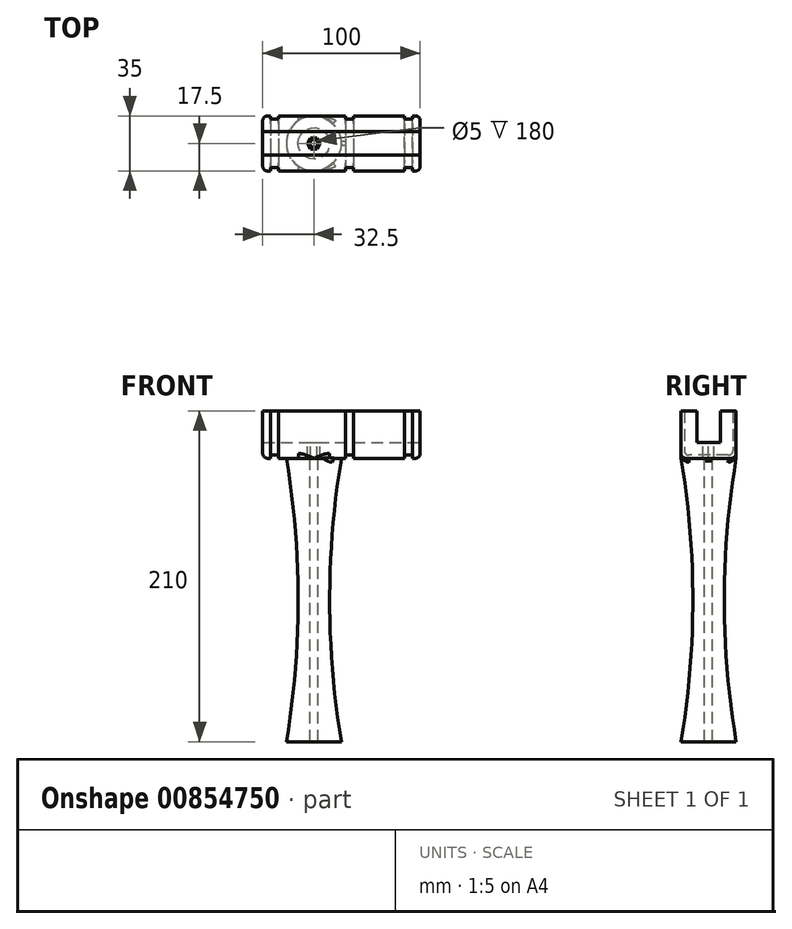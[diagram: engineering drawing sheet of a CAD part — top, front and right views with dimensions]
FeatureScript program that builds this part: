
annotation { "Feature Type Name" : "Feature", "Feature Type Description" : "" }
export const myFeature = defineFeature(function(context is Context, id is Id, definition is map)
    precondition{}
    {
        {
            var Q0;
            Q0=qCreatedBy(makeId("Front.planeOp"),FACE);
            var sketch = newSketch(context, id + "F0", { "sketchPlane" : qUnion([Q0])});
            skLineSegment(sketch, "E0.bottom", {"start": v(50, 15) * mm, "end": v(-50, 15) * mm});
            skLineSegment(sketch, "E0.top", {"start": v(50, -15) * mm, "end": v(-50, -15) * mm});
            skLineSegment(sketch, "E0.left", {"start": v(50, 15) * mm, "end": v(50, -15) * mm});
            skLineSegment(sketch, "E0.right", {"start": v(-50, 15) * mm, "end": v(-50, -15) * mm});
            skPoint(sketch, "E0.middle", {"position": v(0, 0) * mm});
            skLineSegment(sketch, "E1.bottom", {"start": v(-50, 15) * mm, "end": v(50, 15) * mm});
            skLineSegment(sketch, "E1.top", {"start": v(-50, -5) * mm, "end": v(50, -5) * mm});
            skLineSegment(sketch, "E1.left", {"start": v(-50, 15) * mm, "end": v(-50, -5) * mm});
            skLineSegment(sketch, "E1.right", {"start": v(50, 15) * mm, "end": v(50, -5) * mm});
            skSolve(sketch);
        }
        {
            var Q0;
            {var subQ0=sQuery(id+"F0.wireOp",EDGE,"E0.top");Q0=makeQuery(id+"F0.imprint","IMPRINT",FACE,{"disambiguationData":[TD([[makeQuery(id+"F0.imprint","IMPRINT",EDGE,{"derivedFrom":subQ0}),-1.0]])]});}
            var Q1;
            {var subQ0=sQuery(id+"F0.wireOp",EDGE,"E0.bottom");Q1=makeQuery(id+"F0.imprint","IMPRINT",FACE,{"disambiguationData":[TD([[makeQuery(id+"F0.imprint","IMPRINT",EDGE,{"derivedFrom":subQ0}),1.0]])]});}
            extrude(context, id + "F1", {"entities" : qUnion([Q0, Q1]), "endBound" : BoundingType.SYMMETRIC, "depth" : 35 * mm, "offsetDistance" : 25 * mm});
        }
        {
            var Q0;
            {var subQ0=sQuery(id+"F0.wireOp",EDGE,"E0.bottom");Q0=makeQuery(id+"F0.imprint","IMPRINT",FACE,{"disambiguationData":[TD([[makeQuery(id+"F0.imprint","IMPRINT",EDGE,{"derivedFrom":subQ0}),1.0]])]});}
            extrude(context, id + "F2", {"entities" : qUnion([Q0]), "operationType" : NewBodyOperationType.REMOVE, "endBound" : BoundingType.SYMMETRIC, "oppositeDirection" : true, "depth" : 15 * mm, "offsetDistance" : 25 * mm});
        }
        {
            var Q0;
            Q0=makeQuery(id+"F1.opExtrude","SWEPT_FACE",FACE,{"disambiguationData":[OSD([sQuery(id+"F0.wireOp",EDGE,"E0.top")])]});
            var sketch = newSketch(context, id + "F3", { "sketchPlane" : qUnion([Q0])});
            skCircle(sketch, "E2", {"center": v(-17.5, 0) * mm, "radius": 17.5 * mm});
            skPoint(sketch, "E3", {"position": v(-35, 0) * mm});
            skPoint(sketch, "E3.positionSnap0", {"position": v(-50, 0) * mm});
            skPoint(sketch, "E4", {"position": v(-42.5, 0) * mm});
            skLineSegment(sketch, "E5", {"start": v(-17.5, 0) * mm, "end": v(-17.5, 22.7) * mm, "construction": true});
            skPoint(sketch, "E6.MirrorP", {"position": v(7.5, 0) * mm});
            skPoint(sketch, "E7.MirrorP", {"position": v(42.5, 0) * mm});
            skSolve(sketch);
        }
        {
            var Q0;
            Q0=makeQuery(id+"F2.boolean.opBoolean","COPY",FACE,{"derivedFrom":makeQuery(id+"F2.opExtrude","SWEPT_FACE",FACE,{"disambiguationData":[OSD([sQuery(id+"F0.wireOp",EDGE,"E1.top")])]})});
            var sketch = newSketch(context, id + "F4", { "sketchPlane" : qUnion([Q0])});
            skPoint(sketch, "E8.0", {"position": v(-17.5, 0) * mm});
            skCircle(sketch, "E9", {"center": v(-17.5, 0) * mm, "radius": 2.5 * mm});
            skCircle(sketch, "E10.cCircle", {"center": v(-17.5, 0) * mm, "radius": 4 * mm, "construction": true});
            skLineSegment(sketch, "E10.0", {"start": v(-21.5, 0) * mm, "end": v(-19.5, 3.46) * mm});
            skLineSegment(sketch, "E10.1", {"start": v(-19.5, 3.46) * mm, "end": v(-15.5, 3.46) * mm});
            skLineSegment(sketch, "E10.2", {"start": v(-15.5, 3.46) * mm, "end": v(-13.5, 0) * mm});
            skLineSegment(sketch, "E10.3", {"start": v(-13.5, 0) * mm, "end": v(-15.5, -3.46) * mm});
            skLineSegment(sketch, "E10.4", {"start": v(-15.5, -3.46) * mm, "end": v(-19.5, -3.46) * mm});
            skLineSegment(sketch, "E10.5", {"start": v(-19.5, -3.46) * mm, "end": v(-21.5, 0) * mm});
            skSolve(sketch);
        }
        {
            var Q0;
            Q0=makeQuery(id+"F4.imprint","IMPRINT",FACE,{"disambiguationData":[TD([[makeQuery(id+"F4.imprint","IMPRINT",EDGE,{"derivedFrom":sQuery(id+"F4.wireOp",EDGE,"E9")}),-1.0]])]});
            extrude(context, id + "F5", {"entities" : qUnion([Q0]), "operationType" : NewBodyOperationType.REMOVE, "oppositeDirection" : true, "depth" : 10 * mm, "offsetDistance" : 25 * mm});
        }
        {
            var Q0;
            Q0=makeQuery(id+"F4.imprint","IMPRINT",FACE,{"disambiguationData":[TD([[makeQuery(id+"F4.imprint","IMPRINT",EDGE,{"derivedFrom":sQuery(id+"F4.wireOp",EDGE,"E9")}),1.0]])]});
            extrude(context, id + "F6", {"entities" : qUnion([Q0]), "operationType" : NewBodyOperationType.REMOVE, "endBound" : BoundingType.THROUGH_ALL, "oppositeDirection" : true, "depth" : 25 * mm, "offsetDistance" : 25 * mm});
        }
        {
            var Q0;
            {var subQ0=sQuery(id+"F3.wireOp",EDGE,"E2");var subQ1=sQuery(id+"F0.wireOp",EDGE,"E0.top");var subQ2=makeQuery(id+"F3.imprint","INTERSECT",VERTEX,{"derivedFrom":[makeQuery(id+"F1.opExtrude","CAP_EDGE",EDGE,{"disambiguationData":[OSD([subQ1])],"isStart":true}),subQ0]});Q0=makeQuery(id+"F3.imprint","IMPRINT",FACE,{"disambiguationData":[TD([[makeQuery(id+"F3.imprint","IMPRINT",EDGE,{"disambiguationData":[TD([[subQ2,1.0]])],"derivedFrom":subQ0}),1.0]])]});}
            cPlane(context, id + "F7", {"entities" : qUnion([Q0]), "cplaneType" : CPlaneType.OFFSET, "offset" : 180 * mm, "width" : 150 * mm, "height" : 150 * mm});
        }
        {
            var Q0;
            Q0=qCreatedBy(id+"F7.planeOp",FACE);
            var sketch = newSketch(context, id + "F8", { "sketchPlane" : qUnion([Q0])});
            skPoint(sketch, "E11.0", {"position": v(-17.5, 0) * mm});
            skCircle(sketch, "E12", {"center": v(-17.5, 0) * mm, "radius": 17.5 * mm});
            skSolve(sketch);
        }
        {
            var Q0;
            {var subQ0=sQuery(id+"F3.wireOp",EDGE,"E2");var subQ1=sQuery(id+"F0.wireOp",EDGE,"E0.top");var subQ2=makeQuery(id+"F3.imprint","INTERSECT",VERTEX,{"derivedFrom":[makeQuery(id+"F1.opExtrude","CAP_EDGE",EDGE,{"disambiguationData":[OSD([subQ1])],"isStart":true}),subQ0]});Q0=makeQuery(id+"F3.imprint","IMPRINT",FACE,{"disambiguationData":[TD([[makeQuery(id+"F3.imprint","IMPRINT",EDGE,{"disambiguationData":[TD([[subQ2,1.0]])],"derivedFrom":subQ0}),1.0]])]});}
            cPlane(context, id + "F9", {"entities" : qUnion([Q0]), "cplaneType" : CPlaneType.OFFSET, "offset" : 90 * mm, "width" : 150 * mm, "height" : 150 * mm});
        }
        {
            var Q0;
            Q0=qCreatedBy(id+"F9.planeOp",FACE);
            var sketch = newSketch(context, id + "F10", { "sketchPlane" : qUnion([Q0])});
            skPoint(sketch, "E13.0", {"position": v(-17.5, 0) * mm});
            skCircle(sketch, "E14", {"center": v(-17.5, 0) * mm, "radius": 10 * mm});
            skSolve(sketch);
        }
        {
            var Q0;
            Q0=qCreatedBy(makeId("Front.planeOp"),FACE);
            var sketch = newSketch(context, id + "F11", { "sketchPlane" : qUnion([Q0])});
            skLineSegment(sketch, "E15.0", {"start": v(0, -15) * mm, "end": v(-35, -15) * mm});
            skLineSegment(sketch, "E16.0", {"start": v(-7.5, -105) * mm, "end": v(-27.5, -105) * mm, "construction": true});
            skLineSegment(sketch, "E17.0", {"start": v(0, -195) * mm, "end": v(-35, -195) * mm});
            skArc(sketch, "E18", {"start": v(-35, -195) * mm, "mid": v(-27.5, -105) * mm, "end": v(-35, -15) * mm});
            skLineSegment(sketch, "E19", {"start": v(-17.5, -195) * mm, "end": v(-17.5, -15) * mm});
            skSolve(sketch);
        }
        {
            var Q0;
            {var subQ0=sQuery(id+"F11.wireOp",EDGE,"E18");Q0=makeQuery(id+"F11.imprint","IMPRINT",FACE,{"disambiguationData":[TD([[makeQuery(id+"F11.imprint","IMPRINT",EDGE,{"derivedFrom":subQ0}),-1.0]])]});}
            var Q1;
            Q1=sQuery(id+"F11.wireOp",EDGE,"E19");
            revolve(context, id + "F12", {"operationType" : NewBodyOperationType.ADD, "surfaceOperationType" : NewSurfaceOperationType.NEW, "entities" : qUnion([Q0]), "axis" : qUnion([Q1]), "revolveType" : RevolveType.FULL});
        }
        {
            var Q0;
            Q0=makeQuery(id+"F4.imprint","IMPRINT",FACE,{"disambiguationData":[TD([[makeQuery(id+"F4.imprint","IMPRINT",EDGE,{"derivedFrom":sQuery(id+"F4.wireOp",EDGE,"E9")}),1.0]])]});
            extrude(context, id + "F13", {"entities" : qUnion([Q0]), "operationType" : NewBodyOperationType.REMOVE, "endBound" : BoundingType.THROUGH_ALL, "oppositeDirection" : true, "depth" : 25 * mm, "offsetDistance" : 25 * mm});
        }
        {
            var Q0;
            Q0=sQuery(id+"F3.wireOp",VERTEX,"E4");
            var Q1;
            Q1=qCreatedBy(makeId("Right.planeOp"),FACE);
            cPlane(context, id + "F14", {"entities" : qUnion([Q0, Q1]), "cplaneType" : CPlaneType.PLANE_POINT, "offset" : 25 * mm, "width" : 150 * mm, "height" : 150 * mm});
        }
        {
            var Q0;
            Q0=qCreatedBy(id+"F14.planeOp",FACE);
            var sketch = newSketch(context, id + "F15", { "sketchPlane" : qUnion([Q0])});
            skLineSegment(sketch, "E20.0", {"start": v(15.5, 15) * mm, "end": v(15.5, -13) * mm});
            skLineSegment(sketch, "E20.1", {"start": v(15.5, -13) * mm, "end": v(-15.5, -13) * mm});
            skLineSegment(sketch, "E20.2", {"start": v(-15.5, 15) * mm, "end": v(-15.5, -13) * mm});
            skLineSegment(sketch, "E21.0", {"start": v(-17.5, 15) * mm, "end": v(-17.5, -15) * mm});
            skLineSegment(sketch, "E22.0", {"start": v(-17.5, 15) * mm, "end": v(-7.5, 15) * mm});
            skLineSegment(sketch, "E23.0", {"start": v(17.5, -15) * mm, "end": v(-17.5, -15) * mm});
            skLineSegment(sketch, "E24.0", {"start": v(17.5, 15) * mm, "end": v(17.5, -15) * mm});
            skLineSegment(sketch, "E25.0", {"start": v(7.5, 15) * mm, "end": v(17.5, 15) * mm});
            skSolve(sketch);
        }
        {
            var Q0;
            {var subQ2=sQuery(id+"F15.wireOp",EDGE,"E20.0");Q0=makeQuery(id+"F15.imprint","IMPRINT",FACE,{"disambiguationData":[TD([[makeQuery(id+"F15.imprint","IMPRINT",EDGE,{"derivedFrom":subQ2}),1.0]])]});}
            extrude(context, id + "F16", {"entities" : qUnion([Q0]), "operationType" : NewBodyOperationType.REMOVE, "endBound" : BoundingType.SYMMETRIC, "oppositeDirection" : true, "depth" : 5 * mm, "offsetDistance" : 25 * mm});
        }
        {
            var Q0;
            Q0=sQuery(id+"F3.wireOp",VERTEX,"E7.MirrorP");
            var Q1;
            Q1=qCreatedBy(makeId("Right.planeOp"),FACE);
            cPlane(context, id + "F17", {"entities" : qUnion([Q0, Q1]), "cplaneType" : CPlaneType.PLANE_POINT, "offset" : 25 * mm, "width" : 150 * mm, "height" : 150 * mm});
        }
        {
            var Q0;
            Q0=qCreatedBy(makeId("Right.planeOp"),FACE);
            var Q1;
            Q1=sQuery(id+"F3.wireOp",VERTEX,"E6.MirrorP");
            cPlane(context, id + "F18", {"entities" : qUnion([Q0, Q1]), "cplaneType" : CPlaneType.PLANE_POINT, "offset" : 25 * mm, "width" : 150 * mm, "height" : 150 * mm});
        }
        {
            var Q0;
            Q0=qCreatedBy(id+"F17.planeOp",FACE);
            var sketch = newSketch(context, id + "F19", { "sketchPlane" : qUnion([Q0])});
            skLineSegment(sketch, "E26.0", {"start": v(15.5, 15) * mm, "end": v(15.5, -13) * mm});
            skLineSegment(sketch, "E26.1", {"start": v(15.5, -13) * mm, "end": v(-15.5, -13) * mm});
            skLineSegment(sketch, "E26.2", {"start": v(-15.5, 15) * mm, "end": v(-15.5, -13) * mm});
            skLineSegment(sketch, "E27.0", {"start": v(-17.5, 15) * mm, "end": v(-17.5, -15) * mm});
            skLineSegment(sketch, "E28.0", {"start": v(17.5, 15) * mm, "end": v(17.5, -15) * mm});
            skLineSegment(sketch, "E29", {"start": v(-15.5, 15) * mm, "end": v(-17.5, 15) * mm});
            skLineSegment(sketch, "E30", {"start": v(-17.5, -15) * mm, "end": v(17.5, -15) * mm});
            skLineSegment(sketch, "E31", {"start": v(17.5, 15) * mm, "end": v(15.5, 15) * mm});
            skSolve(sketch);
        }
        {
            var Q0;
            Q0=makeQuery(id+"F19.imprint","IMPRINT",FACE,{"disambiguationData":[TD([[makeQuery(id+"F19.imprint","IMPRINT",EDGE,{"derivedFrom":sQuery(id+"F19.wireOp",EDGE,"E26.0")}),1.0]])]});
            extrude(context, id + "F20", {"entities" : qUnion([Q0]), "operationType" : NewBodyOperationType.REMOVE, "endBound" : BoundingType.SYMMETRIC, "oppositeDirection" : true, "depth" : 5 * mm, "offsetDistance" : 25 * mm});
        }
        {
            var Q0;
            Q0=qCreatedBy(id+"F18.planeOp",FACE);
            var sketch = newSketch(context, id + "F21", { "sketchPlane" : qUnion([Q0])});
            skLineSegment(sketch, "E32.0", {"start": v(-15.5, 15) * mm, "end": v(-15.5, -13) * mm});
            skLineSegment(sketch, "E32.1", {"start": v(15.5, -13) * mm, "end": v(-15.5, -13) * mm});
            skLineSegment(sketch, "E32.2", {"start": v(15.5, 15) * mm, "end": v(15.5, -13) * mm});
            skLineSegment(sketch, "E33.0", {"start": v(17.5, 15) * mm, "end": v(17.5, -15) * mm});
            skLineSegment(sketch, "E33.1", {"start": v(17.5, -15) * mm, "end": v(-17.5, -15) * mm});
            skLineSegment(sketch, "E33.2", {"start": v(-17.5, 15) * mm, "end": v(-17.5, -15) * mm});
            skLineSegment(sketch, "E33.3", {"start": v(-17.5, 15) * mm, "end": v(-7.5, 15) * mm});
            skLineSegment(sketch, "E33.4", {"start": v(7.5, 15) * mm, "end": v(17.5, 15) * mm});
            skSolve(sketch);
        }
        {
            var Q0;
            {var subQ2=sQuery(id+"F21.wireOp",EDGE,"E32.0");Q0=makeQuery(id+"F21.imprint","IMPRINT",FACE,{"disambiguationData":[TD([[makeQuery(id+"F21.imprint","IMPRINT",EDGE,{"derivedFrom":subQ2}),-1.0]])]});}
            extrude(context, id + "F22", {"entities" : qUnion([Q0]), "operationType" : NewBodyOperationType.REMOVE, "oppositeDirection" : true, "depth" : 5 * mm, "offsetDistance" : 25 * mm});
        }
        {
            var Q0;
            Q0=makeQuery(id+"F16.boolean.opBoolean","COPY",EDGE,{"derivedFrom":makeQuery(id+"F16.opExtrude","SWEPT_EDGE",EDGE,{"disambiguationData":[OSD([sQuery(id+"F15.wireOp",EDGE,"E20.2"),sQuery(id+"F15.wireOp",EDGE,"E22.0")])]})});
            var Q1;
            Q1=makeQuery(id+"F16.boolean.opBoolean","COPY",EDGE,{"derivedFrom":makeQuery(id+"F16.opExtrude","SWEPT_EDGE",EDGE,{"disambiguationData":[OSD([sQuery(id+"F15.wireOp",EDGE,"E20.0"),sQuery(id+"F15.wireOp",EDGE,"E25.0")])]})});
            var Q2;
            Q2=makeQuery(id+"F16.boolean.opBoolean","COPY",EDGE,{"derivedFrom":makeQuery(id+"F16.opExtrude","SWEPT_EDGE",EDGE,{"disambiguationData":[OSD([sQuery(id+"F15.wireOp",EDGE,"E20.1"),sQuery(id+"F15.wireOp",EDGE,"E20.2")])]})});
            var Q3;
            Q3=makeQuery(id+"F16.boolean.opBoolean","COPY",EDGE,{"derivedFrom":makeQuery(id+"F16.opExtrude","SWEPT_EDGE",EDGE,{"disambiguationData":[OSD([sQuery(id+"F15.wireOp",EDGE,"E20.0"),sQuery(id+"F15.wireOp",EDGE,"E20.1")])]})});
            var Q4;
            Q4=makeQuery(id+"F22.boolean.opBoolean","COPY",EDGE,{"derivedFrom":makeQuery(id+"F22.opExtrude","SWEPT_EDGE",EDGE,{"disambiguationData":[OSD([sQuery(id+"F21.wireOp",EDGE,"E32.0"),sQuery(id+"F21.wireOp",EDGE,"E32.1")])]})});
            var Q5;
            Q5=makeQuery(id+"F22.boolean.opBoolean","COPY",EDGE,{"derivedFrom":makeQuery(id+"F22.opExtrude","SWEPT_EDGE",EDGE,{"disambiguationData":[OSD([sQuery(id+"F21.wireOp",EDGE,"E32.0"),sQuery(id+"F21.wireOp",EDGE,"E33.3")])]})});
            var Q6;
            Q6=makeQuery(id+"F22.boolean.opBoolean","COPY",EDGE,{"derivedFrom":makeQuery(id+"F22.opExtrude","SWEPT_EDGE",EDGE,{"disambiguationData":[OSD([sQuery(id+"F21.wireOp",EDGE,"E32.1"),sQuery(id+"F21.wireOp",EDGE,"E32.2")])]})});
            var Q7;
            Q7=makeQuery(id+"F20.boolean.opBoolean","COPY",EDGE,{"derivedFrom":makeQuery(id+"F20.opExtrude","SWEPT_EDGE",EDGE,{"disambiguationData":[OSD([sQuery(id+"F19.wireOp",EDGE,"E26.0"),sQuery(id+"F19.wireOp",EDGE,"E26.1")])]})});
            var Q8;
            Q8=makeQuery(id+"F20.boolean.opBoolean","COPY",EDGE,{"derivedFrom":makeQuery(id+"F20.opExtrude","SWEPT_EDGE",EDGE,{"disambiguationData":[OSD([sQuery(id+"F19.wireOp",EDGE,"E26.1"),sQuery(id+"F19.wireOp",EDGE,"E26.2")])]})});
            var Q9;
            Q9=makeQuery(id+"F20.boolean.opBoolean","COPY",EDGE,{"derivedFrom":makeQuery(id+"F20.opExtrude","SWEPT_EDGE",EDGE,{"disambiguationData":[OSD([sQuery(id+"F19.wireOp",EDGE,"E26.2"),sQuery(id+"F19.wireOp",EDGE,"E29")])]})});
            var Q10;
            Q10=makeQuery(id+"F20.boolean.opBoolean","COPY",EDGE,{"derivedFrom":makeQuery(id+"F20.opExtrude","SWEPT_EDGE",EDGE,{"disambiguationData":[OSD([sQuery(id+"F19.wireOp",EDGE,"E26.0"),sQuery(id+"F19.wireOp",EDGE,"E31")])]})});
            var Q11;
            Q11=makeQuery(id+"F22.boolean.opBoolean","COPY",EDGE,{"derivedFrom":makeQuery(id+"F22.opExtrude","SWEPT_EDGE",EDGE,{"disambiguationData":[OSD([sQuery(id+"F21.wireOp",EDGE,"E32.2"),sQuery(id+"F21.wireOp",EDGE,"E33.4")])]})});
            fillet(context, id + "F23", {"entities" : qUnion([Q0, Q1, Q2, Q3, Q4, Q5, Q6, Q7, Q8, Q9, Q10, Q11]), "radius" : 3 * mm, "tangentPropagation" : true, "allowEdgeOverflow" : false});
        }
        {
            var Q0;
            {var subQ0=sQuery(id+"F0.wireOp",EDGE,"E0.right");var subQ1=sQuery(id+"F0.wireOp",EDGE,"E0.top");var subQ4=makeQuery(id+"F12.opRevolve","SWEPT_FACE",FACE,{"disambiguationData":[OSD([sQuery(id+"F11.wireOp",EDGE,"E18")])]});Q0=makeQuery(id+"F16.boolean.opBoolean","SPLIT",EDGE,{"disambiguationData":[TD([subQ4])],"derivedFrom":makeQuery(id+"F12.boolean.opBoolean","SPLIT",EDGE,{"disambiguationData":[TD([makeQuery(id+"F1.opExtrude","SWEPT_FACE",FACE,{"disambiguationData":[OSD([subQ0])]})])],"derivedFrom":makeQuery(id+"F1.opExtrude","CAP_EDGE",EDGE,{"disambiguationData":[OSD([subQ1])],"isStart":true})})});}
            var Q1;
            {var subQ0=sQuery(id+"F0.wireOp",EDGE,"E0.left");var subQ1=sQuery(id+"F0.wireOp",EDGE,"E0.top");var subQ3=makeQuery(id+"F20.opExtrude","CAP_FACE",FACE,{"disambiguationData":[OSD([sQuery(id+"F19.wireOp",EDGE,"E26.0"),sQuery(id+"F19.wireOp",EDGE,"E26.1"),sQuery(id+"F19.wireOp",EDGE,"E26.2"),sQuery(id+"F19.wireOp",EDGE,"E27.0"),sQuery(id+"F19.wireOp",EDGE,"E28.0"),sQuery(id+"F19.wireOp",EDGE,"E29"),sQuery(id+"F19.wireOp",EDGE,"E30"),sQuery(id+"F19.wireOp",EDGE,"E31")])],"isStart":false});var subQ5=makeQuery(id+"F12.opRevolve","SWEPT_FACE",FACE,{"disambiguationData":[OSD([sQuery(id+"F11.wireOp",EDGE,"E18")])]});Q1=makeQuery(id+"F22.boolean.opBoolean","SPLIT",EDGE,{"disambiguationData":[TD([makeQuery(id+"F20.boolean.opBoolean","COPY",FACE,{"derivedFrom":subQ3})])],"derivedFrom":makeQuery(id+"F20.boolean.opBoolean","SPLIT",EDGE,{"disambiguationData":[TD([subQ5])],"derivedFrom":makeQuery(id+"F12.boolean.opBoolean","SPLIT",EDGE,{"disambiguationData":[TD([makeQuery(id+"F1.opExtrude","SWEPT_FACE",FACE,{"disambiguationData":[OSD([subQ0])]})])],"derivedFrom":makeQuery(id+"F1.opExtrude","CAP_EDGE",EDGE,{"disambiguationData":[OSD([subQ1])],"isStart":true})})})});}
            var Q2;
            {var subQ0=sQuery(id+"F0.wireOp",EDGE,"E0.left");var subQ1=sQuery(id+"F0.wireOp",EDGE,"E0.top");var subQ4=makeQuery(id+"F1.opExtrude","SWEPT_FACE",FACE,{"disambiguationData":[OSD([subQ0])]});Q2=makeQuery(id+"F20.boolean.opBoolean","SPLIT",EDGE,{"disambiguationData":[TD([subQ4])],"derivedFrom":makeQuery(id+"F12.boolean.opBoolean","SPLIT",EDGE,{"disambiguationData":[TD([subQ4])],"derivedFrom":makeQuery(id+"F1.opExtrude","CAP_EDGE",EDGE,{"disambiguationData":[OSD([subQ1])],"isStart":true})})});}
            var Q3;
            Q3=makeQuery(id+"F1.opExtrude","CAP_EDGE",EDGE,{"disambiguationData":[OSD([sQuery(id+"F0.wireOp",EDGE,"E0.left")])],"isStart":true});
            var Q4;
            Q4=makeQuery(id+"F1.opExtrude","CAP_EDGE",EDGE,{"disambiguationData":[OSD([sQuery(id+"F0.wireOp",EDGE,"E0.left")])],"isStart":false});
            var Q5;
            Q5=makeQuery(id+"F1.opExtrude","SWEPT_EDGE",EDGE,{"disambiguationData":[OSD([sQuery(id+"F0.wireOp",EDGE,"E0.top"),sQuery(id+"F0.wireOp",EDGE,"E0.left")])]});
            var Q6;
            {var subQ0=sQuery(id+"F0.wireOp",EDGE,"E0.left");var subQ1=sQuery(id+"F0.wireOp",EDGE,"E0.top");var subQ4=makeQuery(id+"F20.opExtrude","CAP_FACE",FACE,{"disambiguationData":[OSD([sQuery(id+"F19.wireOp",EDGE,"E26.0"),sQuery(id+"F19.wireOp",EDGE,"E26.1"),sQuery(id+"F19.wireOp",EDGE,"E26.2"),sQuery(id+"F19.wireOp",EDGE,"E27.0"),sQuery(id+"F19.wireOp",EDGE,"E28.0"),sQuery(id+"F19.wireOp",EDGE,"E29"),sQuery(id+"F19.wireOp",EDGE,"E30"),sQuery(id+"F19.wireOp",EDGE,"E31")])],"isStart":false});var subQ5=makeQuery(id+"F12.opRevolve","SWEPT_FACE",FACE,{"disambiguationData":[OSD([sQuery(id+"F11.wireOp",EDGE,"E18")])]});Q6=makeQuery(id+"F22.boolean.opBoolean","SPLIT",EDGE,{"disambiguationData":[TD([makeQuery(id+"F20.boolean.opBoolean","COPY",FACE,{"derivedFrom":subQ4})])],"derivedFrom":makeQuery(id+"F20.boolean.opBoolean","SPLIT",EDGE,{"disambiguationData":[TD([subQ5])],"derivedFrom":makeQuery(id+"F12.boolean.opBoolean","SPLIT",EDGE,{"disambiguationData":[TD([makeQuery(id+"F1.opExtrude","SWEPT_FACE",FACE,{"disambiguationData":[OSD([subQ0])]})])],"derivedFrom":makeQuery(id+"F1.opExtrude","CAP_EDGE",EDGE,{"disambiguationData":[OSD([subQ1])],"isStart":false})})})});}
            var Q7;
            Q7=makeQuery(id+"F1.opExtrude","CAP_EDGE",EDGE,{"disambiguationData":[OSD([sQuery(id+"F0.wireOp",EDGE,"E0.right")])],"isStart":true});
            var Q8;
            {var subQ0=sQuery(id+"F0.wireOp",EDGE,"E0.right");var subQ1=sQuery(id+"F0.wireOp",EDGE,"E0.top");var subQ4=makeQuery(id+"F1.opExtrude","SWEPT_FACE",FACE,{"disambiguationData":[OSD([subQ0])]});Q8=makeQuery(id+"F16.boolean.opBoolean","SPLIT",EDGE,{"disambiguationData":[TD([subQ4])],"derivedFrom":makeQuery(id+"F12.boolean.opBoolean","SPLIT",EDGE,{"disambiguationData":[TD([subQ4])],"derivedFrom":makeQuery(id+"F1.opExtrude","CAP_EDGE",EDGE,{"disambiguationData":[OSD([subQ1])],"isStart":true})})});}
            var Q9;
            Q9=makeQuery(id+"F1.opExtrude","SWEPT_EDGE",EDGE,{"disambiguationData":[OSD([sQuery(id+"F0.wireOp",EDGE,"E0.top"),sQuery(id+"F0.wireOp",EDGE,"E0.right")])]});
            var Q10;
            Q10=makeQuery(id+"F1.opExtrude","CAP_EDGE",EDGE,{"disambiguationData":[OSD([sQuery(id+"F0.wireOp",EDGE,"E0.right")])],"isStart":false});
            var Q11;
            {var subQ0=sQuery(id+"F0.wireOp",EDGE,"E0.right");var subQ1=sQuery(id+"F0.wireOp",EDGE,"E0.top");var subQ3=makeQuery(id+"F12.opRevolve","SWEPT_FACE",FACE,{"disambiguationData":[OSD([sQuery(id+"F11.wireOp",EDGE,"E18")])]});Q11=makeQuery(id+"F16.boolean.opBoolean","SPLIT",EDGE,{"disambiguationData":[TD([subQ3])],"derivedFrom":makeQuery(id+"F12.boolean.opBoolean","SPLIT",EDGE,{"disambiguationData":[TD([makeQuery(id+"F1.opExtrude","SWEPT_FACE",FACE,{"disambiguationData":[OSD([subQ0])]})])],"derivedFrom":makeQuery(id+"F1.opExtrude","CAP_EDGE",EDGE,{"disambiguationData":[OSD([subQ1])],"isStart":false})})});}
            var Q12;
            {var subQ0=sQuery(id+"F0.wireOp",EDGE,"E0.left");var subQ1=sQuery(id+"F0.wireOp",EDGE,"E0.top");var subQ4=makeQuery(id+"F1.opExtrude","SWEPT_FACE",FACE,{"disambiguationData":[OSD([subQ0])]});Q12=makeQuery(id+"F20.boolean.opBoolean","SPLIT",EDGE,{"disambiguationData":[TD([subQ4])],"derivedFrom":makeQuery(id+"F12.boolean.opBoolean","SPLIT",EDGE,{"disambiguationData":[TD([subQ4])],"derivedFrom":makeQuery(id+"F1.opExtrude","CAP_EDGE",EDGE,{"disambiguationData":[OSD([subQ1])],"isStart":false})})});}
            var Q13;
            {var subQ0=sQuery(id+"F0.wireOp",EDGE,"E0.right");var subQ1=sQuery(id+"F0.wireOp",EDGE,"E0.top");var subQ4=makeQuery(id+"F1.opExtrude","SWEPT_FACE",FACE,{"disambiguationData":[OSD([subQ0])]});Q13=makeQuery(id+"F16.boolean.opBoolean","SPLIT",EDGE,{"disambiguationData":[TD([subQ4])],"derivedFrom":makeQuery(id+"F12.boolean.opBoolean","SPLIT",EDGE,{"disambiguationData":[TD([subQ4])],"derivedFrom":makeQuery(id+"F1.opExtrude","CAP_EDGE",EDGE,{"disambiguationData":[OSD([subQ1])],"isStart":false})})});}
            fillet(context, id + "F24", {"entities" : qUnion([Q0, Q1, Q2, Q3, Q4, Q5, Q6, Q7, Q8, Q9, Q10, Q11, Q12, Q13]), "radius" : 3 * mm, "tangentPropagation" : true, "allowEdgeOverflow" : false});
        }
        {
            var Q0;
            Q0=makeQuery(id+"F12.boolean.opBoolean","SPLIT",EDGE,{"disambiguationData":[OD(1.0)],"derivedFrom":makeQuery(id+"F12.opRevolve","SWEPT_EDGE",EDGE,{"disambiguationData":[OSD([sQuery(id+"F11.wireOp",EDGE,"E15.0"),sQuery(id+"F11.wireOp",EDGE,"E18")])]})});
            fillet(context, id + "F25", {"entities" : qUnion([Q0]), "radius" : 3 * mm, "tangentPropagation" : true, "allowEdgeOverflow" : false});
        }
    });
